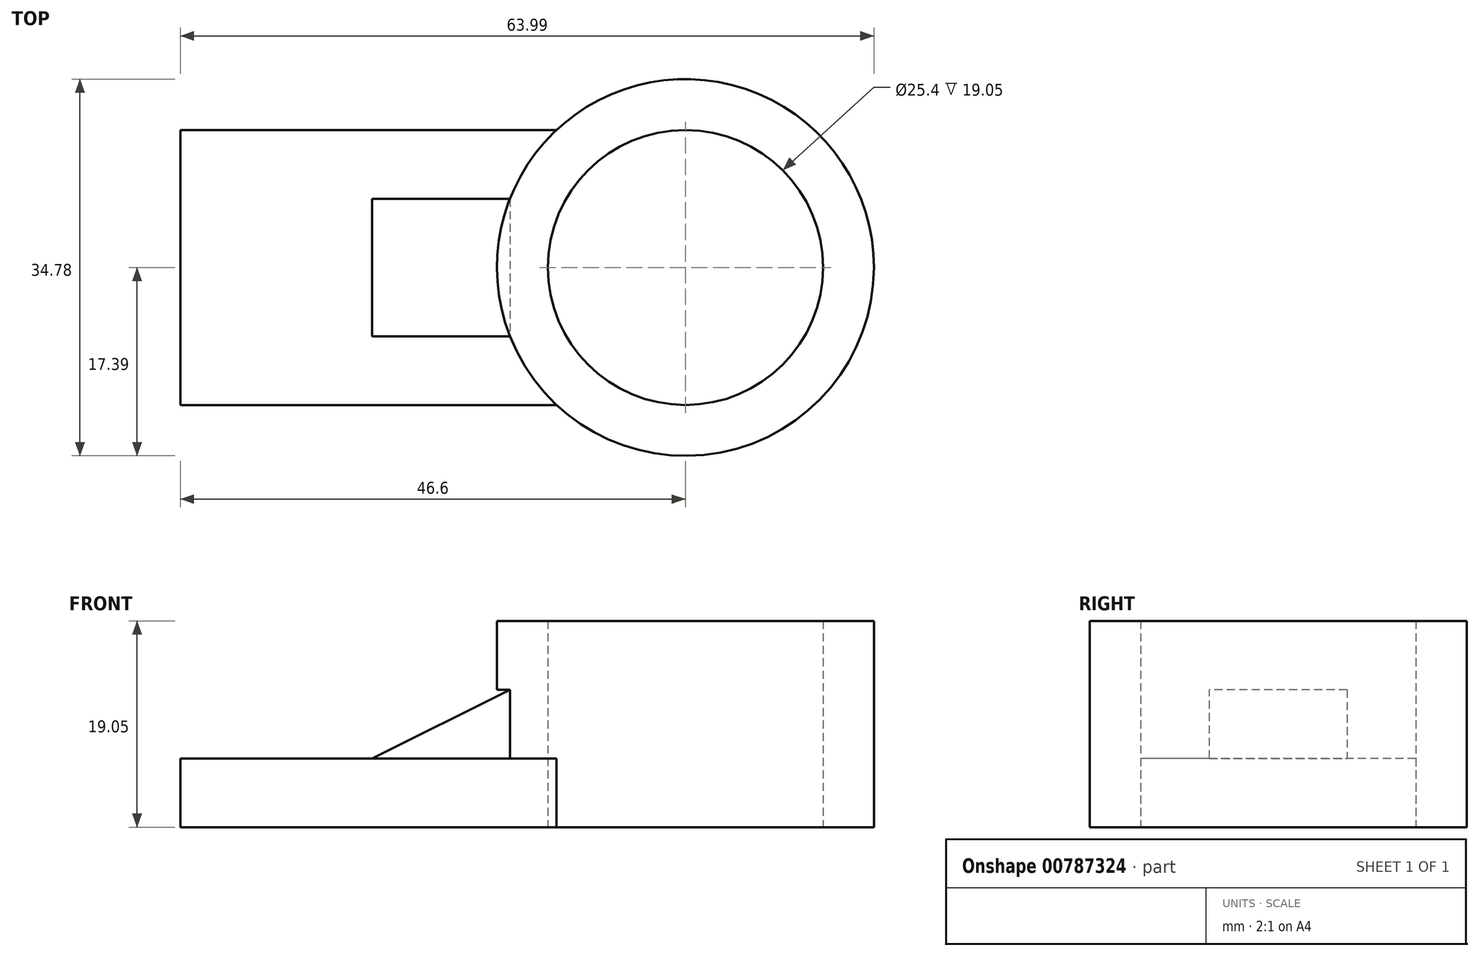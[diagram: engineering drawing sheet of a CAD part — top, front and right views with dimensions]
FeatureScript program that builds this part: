
annotation { "Feature Type Name" : "Feature", "Feature Type Description" : "" }
export const myFeature = defineFeature(function(context is Context, id is Id, definition is map)
    precondition{}
    {
        {
            var Q0;
            Q0=qCreatedBy(makeId("Top.planeOp"),FACE);
            var sketch = newSketch(context, id + "F0", { "sketchPlane" : qUnion([Q0])});
            skCircle(sketch, "E0", {"center": v(0, 0) * mm, "radius": 12.7 * mm});
            skCircle(sketch, "E1", {"center": v(0, 0) * mm, "radius": 17.4 * mm});
            skLineSegment(sketch, "E2", {"start": v(-11.89, -12.7) * mm, "end": v(-46.6, -12.7) * mm});
            skLineSegment(sketch, "E3", {"start": v(-11.89, 12.7) * mm, "end": v(-46.6, 12.7) * mm});
            skLineSegment(sketch, "E4", {"start": v(-46.6, 12.7) * mm, "end": v(-46.6, -12.7) * mm});
            skSolve(sketch);
        }
        {
            var Q0;
            Q0=makeQuery(id+"F0.imprint","IMPRINT",FACE,{"disambiguationData":[TD([[makeQuery(id+"F0.imprint","IMPRINT",EDGE,{"derivedFrom":sQuery(id+"F0.wireOp",EDGE,"E0")}),-1.0]])]});
            extrude(context, id + "F1", {"entities" : qUnion([Q0]), "depth" : 19.05 * mm, "offsetDistance" : 25.4 * mm});
        }
        {
            var Q0;
            {var subQ0=sQuery(id+"F0.wireOp",EDGE,"E2");Q0=makeQuery(id+"F0.imprint","IMPRINT",FACE,{"disambiguationData":[TD([[makeQuery(id+"F0.imprint","IMPRINT",EDGE,{"derivedFrom":subQ0}),-1.0]])]});}
            extrude(context, id + "F2", {"entities" : qUnion([Q0]), "operationType" : NewBodyOperationType.ADD, "depth" : 6.35 * mm, "offsetDistance" : 25.4 * mm});
        }
        {
            var Q0;
            Q0=makeQuery(id+"F2.opExtrude","CAP_FACE",FACE,{"disambiguationData":[OSD([sQuery(id+"F0.wireOp",EDGE,"E1"),sQuery(id+"F0.wireOp",EDGE,"E2"),sQuery(id+"F0.wireOp",EDGE,"E3"),sQuery(id+"F0.wireOp",EDGE,"E4")])],"isStart":false});
            var sketch = newSketch(context, id + "F3", { "sketchPlane" : qUnion([Q0])});
            skLineSegment(sketch, "E5", {"start": v(-28.92, 0) * mm, "end": v(-28.92, 6.35) * mm});
            skLineSegment(sketch, "E6", {"start": v(-28.92, 6.35) * mm, "end": v(-16.2, 6.35) * mm});
            skLineSegment(sketch, "E7", {"start": v(-28.92, 0) * mm, "end": v(-28.92, -6.35) * mm});
            skLineSegment(sketch, "E8", {"start": v(-28.92, -6.35) * mm, "end": v(-16.2, -6.35) * mm});
            skPoint(sketch, "E9.start.orphan", {"position": v(-46.6, 0) * mm});
            skSolve(sketch);
        }
        {
            var Q0;
            Q0=makeQuery(id+"F3.imprint","IMPRINT",FACE,{"disambiguationData":[TD([[makeQuery(id+"F3.imprint","IMPRINT",EDGE,{"derivedFrom":sQuery(id+"F3.wireOp",EDGE,"E5")}),-1.0]])]});
            extrude(context, id + "F4", {"entities" : qUnion([Q0]), "operationType" : NewBodyOperationType.ADD, "depth" : 6.35 * mm, "offsetDistance" : 25.4 * mm});
        }
        {
            var Q0;
            Q0=makeQuery(id+"F4.opExtrude","SWEPT_FACE",FACE,{"disambiguationData":[OSD([sQuery(id+"F3.wireOp",EDGE,"E8")])]});
            var sketch = newSketch(context, id + "F5", { "sketchPlane" : qUnion([Q0])});
            skLineSegment(sketch, "E10", {"start": v(-28.92, 6.35) * mm, "end": v(-16.2, 12.7) * mm});
            skSolve(sketch);
        }
        {
            var Q0;
            Q0=makeQuery(id+"F5.imprint","IMPRINT",FACE,{"disambiguationData":[TD([[makeQuery(id+"F5.imprint","IMPRINT",EDGE,{"derivedFrom":sQuery(id+"F5.wireOp",EDGE,"E10")}),1.0]])]});
            extrude(context, id + "F6", {"entities" : qUnion([Q0]), "operationType" : NewBodyOperationType.REMOVE, "oppositeDirection" : true, "depth" : 25.4 * mm, "offsetDistance" : 25.4 * mm});
        }
    });
